# Revit family: METEOR_MM_60W_4000K_4800LM
name_source: partatom
category: Lighting Fixtures
units: mm (PartAtom-declared; Revit-internal decimal feet)

## family parameters
Always vertical = Yes
Cut with Voids When Loaded = No
Host = Ceiling
Light Source = Yes
OmniClass Number = 23.80.70.11
OmniClass Title = Luminaries for Internal Lighting
Part Type = Normal
Room Calculation Point = No
Round Connector Dimension = Use Diameter
Shared = No

## types (1)
- Type 1
    Alimentation Driver = AC 220-240V
    Alimentation luminaire = 1500mA / 25-42V dc
    Angle d'éclairage = 120°
    Color Filter = 16777215
    Default Elevation = 0 mm  [stored 0 ft]
    Diffuseur = Acrylique
    Dimensions = Ø600 mm, H : 98 mm
    Dimming Lamp Color Temperature Shift = <None>
    Driver = Lifud No Flicker
    Fintion = Blanc
    IRC = >80
    Matériau = Corps en métal
    Photometric Web File = google_eulumdat_converter (23).ies
    Puissance nominale = 60W
    Tilt Angle = 90.00°
    Type = Plafonnier
    Type de lampe = LED Hongli

note: [stored X ft] marks values corroborated as IEEE doubles in the binary element streams (Revit-internal decimal feet)

## geometry (parser evidence)
native form markers: Sweep x3
no freeform markers — native parametric forms only
